# Revit family: NBS_AndersonGECLtd_Snks_SeriesA_Single
name_source: partatom
category: Plumbing Fixtures
revit_build: Autodesk Revit 2017 (Build: 20160225_1515(x64)
units: mm (PartAtom-declared; Revit-internal decimal feet)

## family parameters
Cut with Voids When Loaded = No
Host = Face
Part Type = Normal
Room Calculation Point = No
Round Connector Dimension = Use Diameter
Shared = No

## types (8) — shared parameters
AssetType = Fixed
BowlDepth = 400 mm  [stored 1.31234 ft]
CW Connection = No
Category = Pr_40_20_96_81:Sinks
CodePerformance = EN 1.4301
CornerRadius = 15 mm  [stored 0.0492126 ft]
Description = Single bowled stainless steel sink
DrainDiameter = 89 mm  [stored 0.291995 ft]
DurationUnit = year
ExpectedLife = 30 years
Features = Can be integrated with stainless steel worktops, basket strainer waste and , overflow fittings included
Finish = Bright satin
FixingOptions = Inset, undermount, flushmount
FlatFlange = 20 mm with corner radius of 10 mm
Form = Single bowled sink
Grade = EN 1.4301
HW Connection = No
IfcExportAs = IfcSanitaryTerminalType
IfcExportType = SINK
ManufacturerName = Anderson, GEC Ltd
ManufacturerURL = www.gecanderson.co.uk
Material = Stainless steel
Mounting = Inset, undermount, flushmount
NBSCertification = www.nationalbimlibrary.com/cert/3d4h0m4t
NBSDescription = Sinks
NBSReference = 45-35-70/344
NominalLength = 400 mm  [stored 1.31234 ft]
ProductInformation = http://www.gecanderson.co.uk
Shape = Rectangle
SinkMaterial = NBS_Concept
SinkType = Other
SustainabilityPerformance = 100% Recyclable
Uniclass2015Code = Pr_40_20_96_81
Uniclass2015Title = Sinks
Uniclass2015Version = Products v1.11
Vent Connection = No
Version = 1
WarrantyDurationUnit = year
Waste Connection = Yes
zero-valued in all types: Default Elevation, DrainSize, WFU

## per-type parameters (varying)
| type | BIMObjectName | BowlHeight | BowlWidth | Name | NominalHeight | NominalWidth | Size |
| A18 | NBS_AndersonGECLtd_Sinks_A18 | 170 mm  [stored 0.557743 ft] | 180 mm  [stored 0.590551 ft] | Sinks_A18_AndersonGECLtd | 170 mm  [stored 0.557743 ft] | 180 mm  [stored 0.590551 ft] | 220 x 440 x 170 mm |
| A23 | NBS_AndersonGECLtd_Sinks_A23 | 170 mm  [stored 0.557743 ft] | 230 mm | Sinks_A23_AndersonGECLtd | 170 mm  [stored 0.557743 ft] | 230 mm | 270 x 440 x 170 mm |
| A34 | NBS_AndersonGECLtd_Sinks_A34 | 200 mm | 340 mm | Sinks_A34_AndersonGECLtd | 200 mm | 340 mm | 380 x 440 x 200 mm |
| A40 | NBS_AndersonGECLtd_Sinks_A40 | 200 mm | 400 mm  [stored 1.31234 ft] | Sinks_A40_AndersonGECLtd | 200 mm | 400 mm  [stored 1.31234 ft] | 440 x 440 x 200 mm |
| A45 | NBS_AndersonGECLtd_Sinks_A45 | 200 mm | 450 mm | Sinks_A45_AndersonGECLtd | 200 mm | 450 mm | 490 x 440 x 200 mm |
| A50 | NBS_AndersonGECLtd_Sinks_A50 | 200 mm | 500 mm | Sinks_A50_AndersonGECLtd | 200 mm | 500 mm | 540 x 440 x 200 mm |
| A55 | NBS_AndersonGECLtd_Sinks_A55 | 200 mm | 550 mm | Sinks_A55_AndersonGECLtd | 200 mm | 550 mm | 590 x 440 x 200 mm |
| A70 | NBS_AndersonGECLtd_Sinks_A70 | 200 mm | 700 mm | Sinks_A70_AndersonGECLtd | 200 mm | 700 mm | 740 x 440 x 200 mm |

note: column(s) folded — value = type name in every type: ModelNumber, ModelReference

note: [stored X ft] marks values corroborated as IEEE doubles in the binary element streams (Revit-internal decimal feet)

## geometry (parser evidence)
native form markers: Sweep x2
no freeform markers — native parametric forms only
